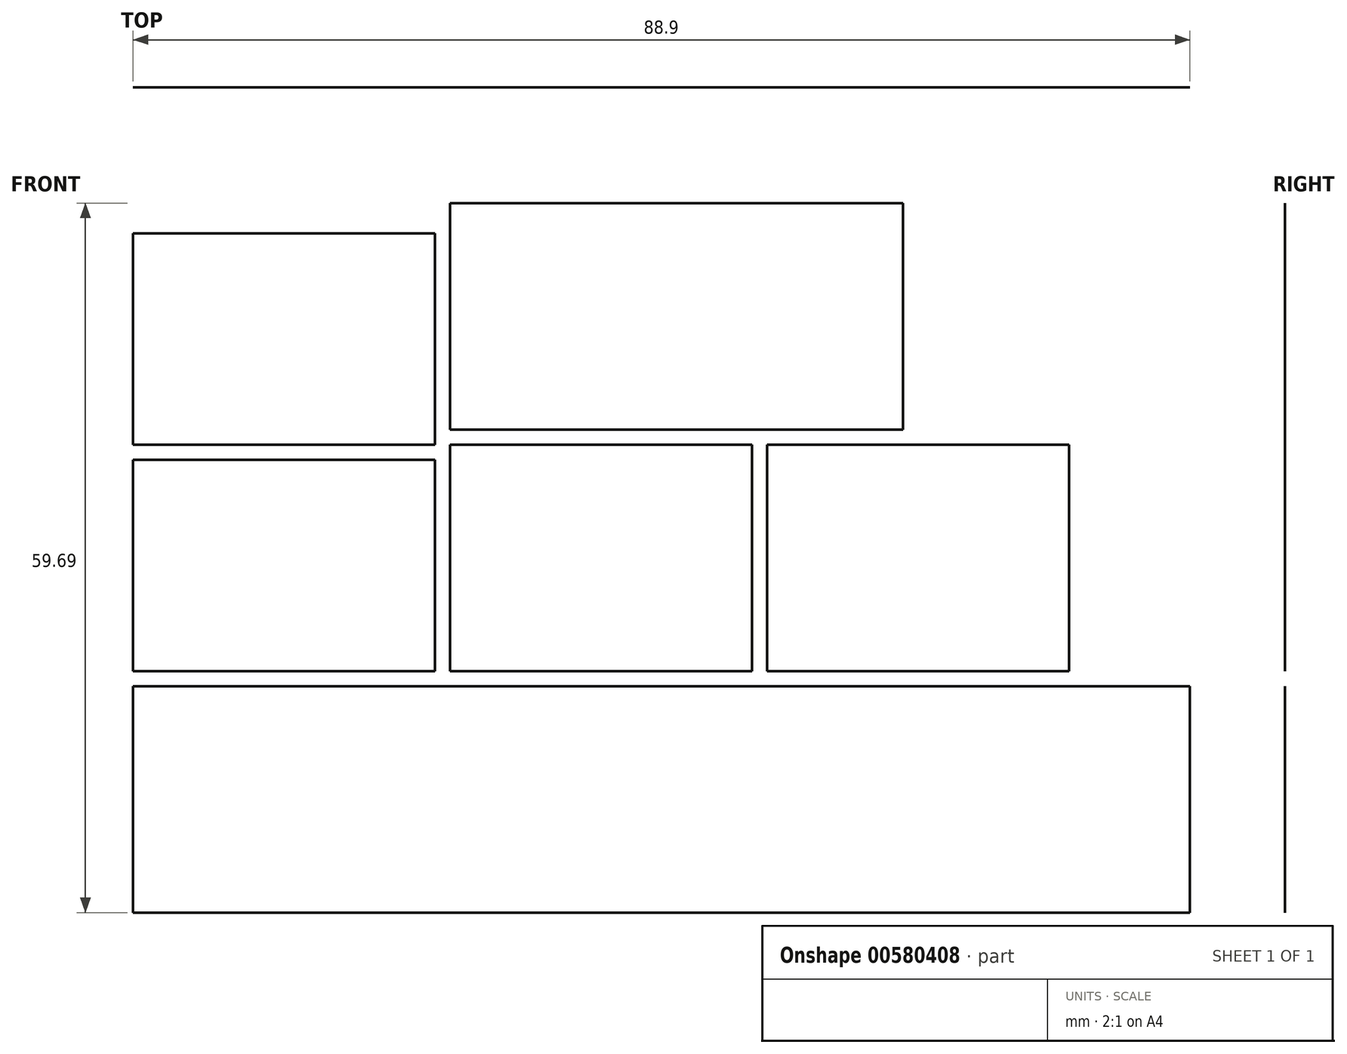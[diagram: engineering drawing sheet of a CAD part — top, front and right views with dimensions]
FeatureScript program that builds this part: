
annotation { "Feature Type Name" : "Feature", "Feature Type Description" : "" }
export const myFeature = defineFeature(function(context is Context, id is Id, definition is map)
    precondition{}
    {
        {
            var Q0;
            Q0=qCreatedBy(makeId("Front.planeOp"),FACE);
            var sketch = newSketch(context, id + "F0", { "sketchPlane" : qUnion([Q0])});
            skLineSegment(sketch, "E0.bottom", {"start": v(-57.35, 43.8) * mm, "end": v(-31.95, 43.8) * mm});
            skLineSegment(sketch, "E0.top", {"start": v(-57.35, 26.01) * mm, "end": v(-31.95, 26.01) * mm});
            skLineSegment(sketch, "E0.left", {"start": v(-57.35, 43.8) * mm, "end": v(-57.35, 26.01) * mm});
            skLineSegment(sketch, "E0.right", {"start": v(-31.95, 43.8) * mm, "end": v(-31.95, 26.01) * mm});
            skLineSegment(sketch, "E1.bottom", {"start": v(-57.35, 24.74) * mm, "end": v(-31.95, 24.74) * mm});
            skLineSegment(sketch, "E1.top", {"start": v(-57.35, 6.96) * mm, "end": v(-31.95, 6.96) * mm});
            skLineSegment(sketch, "E1.left", {"start": v(-57.35, 24.74) * mm, "end": v(-57.35, 6.96) * mm});
            skLineSegment(sketch, "E1.right", {"start": v(-31.95, 24.74) * mm, "end": v(-31.95, 6.96) * mm});
            skLineSegment(sketch, "E2.bottom", {"start": v(-30.68, 46.33) * mm, "end": v(7.42, 46.33) * mm});
            skLineSegment(sketch, "E2.top", {"start": v(-30.68, 27.28) * mm, "end": v(7.42, 27.28) * mm});
            skLineSegment(sketch, "E2.left", {"start": v(-30.68, 46.33) * mm, "end": v(-30.68, 27.28) * mm});
            skLineSegment(sketch, "E2.right", {"start": v(7.42, 46.33) * mm, "end": v(7.42, 27.28) * mm});
            skLineSegment(sketch, "E3.bottom", {"start": v(-57.35, 5.7) * mm, "end": v(31.55, 5.7) * mm});
            skLineSegment(sketch, "E3.top", {"start": v(-57.35, -13.36) * mm, "end": v(31.55, -13.36) * mm});
            skLineSegment(sketch, "E3.left", {"start": v(-57.35, 5.7) * mm, "end": v(-57.35, -13.36) * mm});
            skLineSegment(sketch, "E3.right", {"start": v(31.55, 5.7) * mm, "end": v(31.55, -13.36) * mm});
            skLineSegment(sketch, "E4.bottom", {"start": v(-30.68, 26.01) * mm, "end": v(-5.28, 26.01) * mm});
            skLineSegment(sketch, "E4.top", {"start": v(-30.68, 6.96) * mm, "end": v(-5.28, 6.96) * mm});
            skLineSegment(sketch, "E4.left", {"start": v(-30.68, 26.01) * mm, "end": v(-30.68, 6.96) * mm});
            skLineSegment(sketch, "E4.right", {"start": v(-5.28, 26.01) * mm, "end": v(-5.28, 6.96) * mm});
            skLineSegment(sketch, "E5.bottom", {"start": v(-4, 26.01) * mm, "end": v(21.4, 26.01) * mm});
            skLineSegment(sketch, "E5.top", {"start": v(-4, 6.96) * mm, "end": v(21.4, 6.96) * mm});
            skLineSegment(sketch, "E5.left", {"start": v(-4, 26.01) * mm, "end": v(-4, 6.96) * mm});
            skLineSegment(sketch, "E5.right", {"start": v(21.4, 26.01) * mm, "end": v(21.4, 6.96) * mm});
            skSolve(sketch);
        }
        {
            var Q0;
            Q0=makeQuery(id+"F0.imprint","IMPRINT",FACE,{"disambiguationData":[TD([[makeQuery(id+"F0.imprint","IMPRINT",EDGE,{"derivedFrom":sQuery(id+"F0.wireOp",EDGE,"E0.bottom")}),-1.0]])]});
            var Q1;
            Q1=makeQuery(id+"F0.imprint","IMPRINT",FACE,{"disambiguationData":[TD([[makeQuery(id+"F0.imprint","IMPRINT",EDGE,{"derivedFrom":sQuery(id+"F0.wireOp",EDGE,"E2.bottom")}),-1.0]])]});
            var Q2;
            Q2=makeQuery(id+"F0.imprint","IMPRINT",FACE,{"disambiguationData":[TD([[makeQuery(id+"F0.imprint","IMPRINT",EDGE,{"derivedFrom":sQuery(id+"F0.wireOp",EDGE,"E4.bottom")}),-1.0]])]});
            var Q3;
            Q3=makeQuery(id+"F0.imprint","IMPRINT",FACE,{"disambiguationData":[TD([[makeQuery(id+"F0.imprint","IMPRINT",EDGE,{"derivedFrom":sQuery(id+"F0.wireOp",EDGE,"E1.bottom")}),-1.0]])]});
            var Q4;
            Q4=makeQuery(id+"F0.imprint","IMPRINT",FACE,{"disambiguationData":[TD([[makeQuery(id+"F0.imprint","IMPRINT",EDGE,{"derivedFrom":sQuery(id+"F0.wireOp",EDGE,"E3.bottom")}),-1.0]])]});
            var Q5;
            Q5=makeQuery(id+"F0.imprint","IMPRINT",FACE,{"disambiguationData":[TD([[makeQuery(id+"F0.imprint","IMPRINT",EDGE,{"derivedFrom":sQuery(id+"F0.wireOp",EDGE,"E5.bottom")}),-1.0]])]});
            extrude(context, id + "F1", {"entities" : qUnion([Q0, Q1, Q2, Q3, Q4, Q5]), "depth" : 1 / 203.2 * mm, "offsetDistance" : 25.4 * mm});
        }
    });
